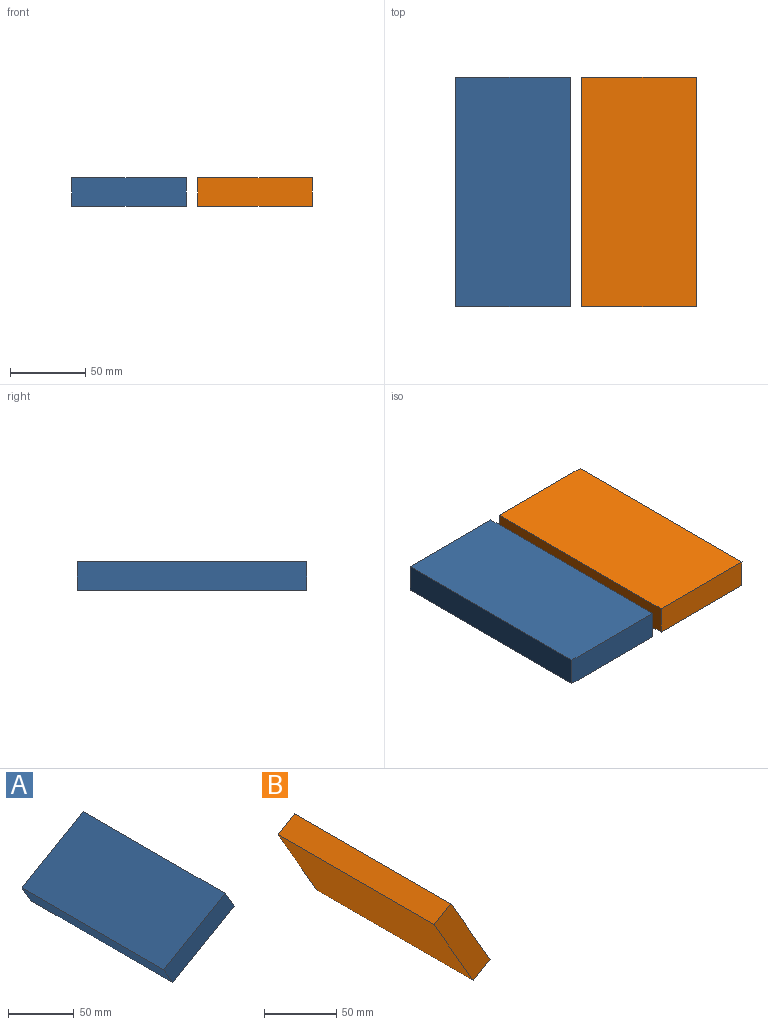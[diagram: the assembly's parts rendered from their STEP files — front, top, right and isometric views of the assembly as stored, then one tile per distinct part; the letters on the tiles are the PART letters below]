
ASSEMBLY  parts=2 mates=3
PART A: 6 faces, bbox 75.5x152.4x54.6 mm
  f0: plane 75.52x54.6mm, normal (0,-1,0), area 1451.6mm2, adj f1,f3,f4,f5
  f1: plane 152.4x16.5mm, normal (-0.87,0,-0.5), area 2903.2mm2, adj f0,f2,f4,f5
  f2: plane 75.52x54.6mm, normal (0,1,0), area 1451.6mm2, adj f1,f3,f4,f5
  f3: plane 152.4x16.5mm, normal (0.87,0,0.5), area 2903.2mm2, adj f0,f2,f4,f5
  f4: plane 152.4x65.99mm, normal (-0.5,0,0.87), area 11612.9mm2, adj f0,f1,f2,f3
  f5: plane 152.4x65.99mm, normal (0.5,0,-0.87), area 11612.9mm2, adj f0,f1,f2,f3
PART B: 6 faces, bbox 54.6x152.4x75.5 mm
  f0: plane 75.52x54.6mm, normal (0,-1,0), area 1451.6mm2, adj f1,f3,f4,f5
  f1: plane 152.4x16.5mm, normal (0.5,0,-0.87), area 2903.2mm2, adj f0,f2,f4,f5
  f2: plane 75.52x54.6mm, normal (0,1,0), area 1451.6mm2, adj f1,f3,f4,f5
  f3: plane 152.4x16.5mm, normal (-0.5,0,0.87), area 2903.2mm2, adj f0,f2,f4,f5
  f4: plane 152.4x65.99mm, normal (-0.87,0,-0.5), area 11612.9mm2, adj f0,f1,f2,f3
  f5: plane 152.4x65.99mm, normal (0.87,0,0.5), area 11612.9mm2, adj f0,f1,f2,f3
PLACE A rot(axis=(0,1,0),30deg) t=(113.68,153.53,0)mm
PLACE B rot(axis=(0,-1,0),60deg) t=(128.27,153.53,81.93)mm
MATE planar A.f0 <-> B.f0  axis (0,-1,0) through (38.1,0,19.05)mm
MATE parallel B.f1 <-> A.f1  axis (1,0,0) through (160.02,76.2,9.53)mm
MATE planar B.f4 <-> A.f5  axis (0,0,-1) through (160.02,76.2,0)mm
